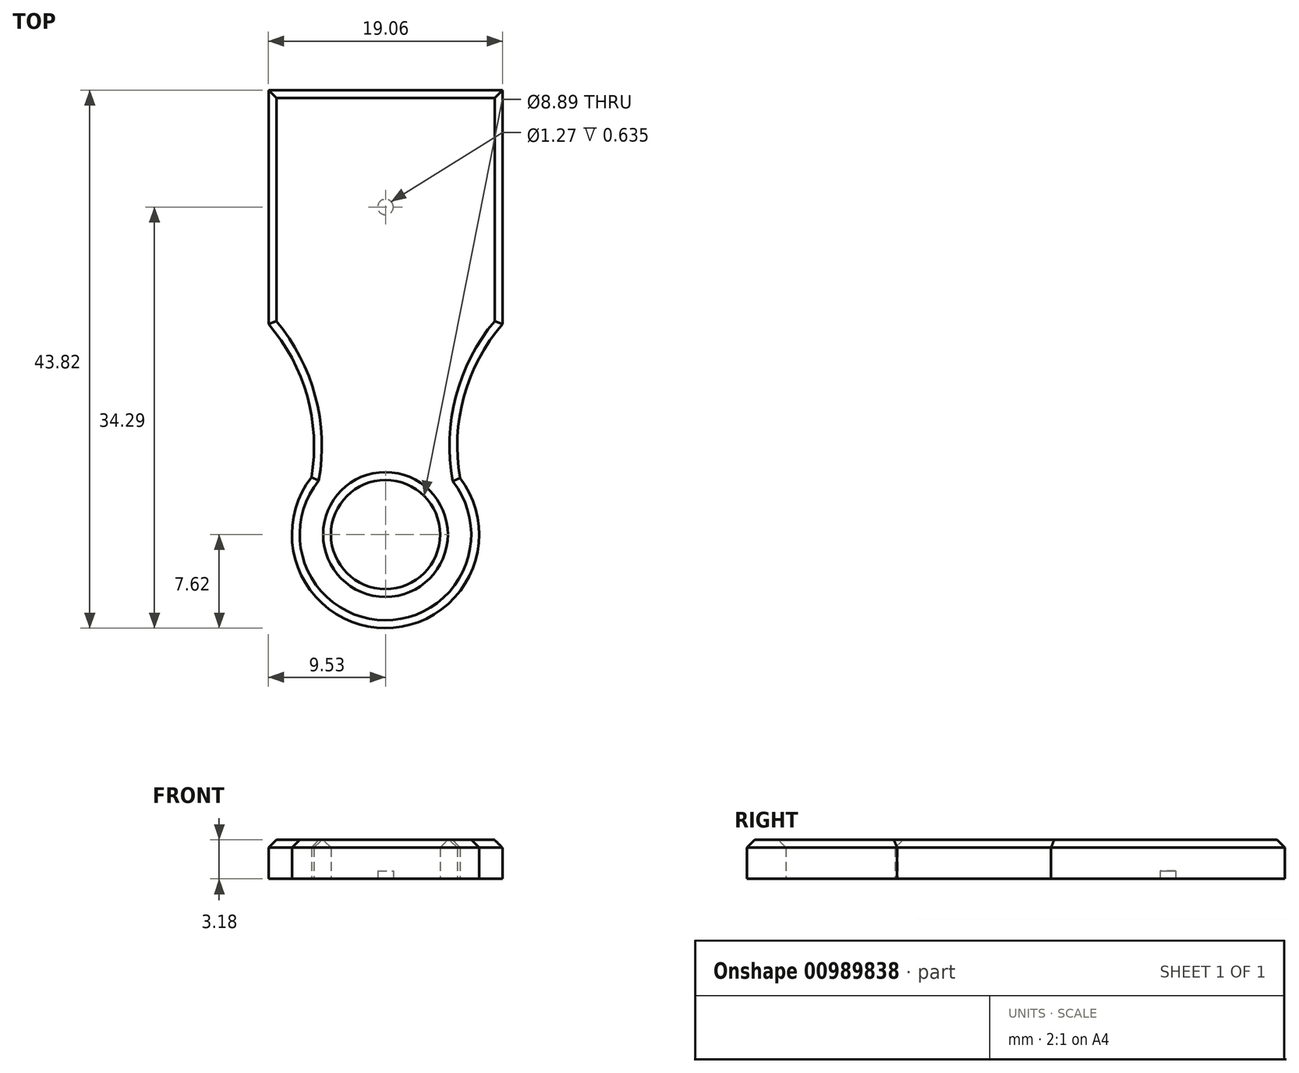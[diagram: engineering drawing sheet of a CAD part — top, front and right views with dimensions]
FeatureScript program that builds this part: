
annotation { "Feature Type Name" : "Feature", "Feature Type Description" : "" }
export const myFeature = defineFeature(function(context is Context, id is Id, definition is map)
    precondition{}
    {
        {
            var Q0;
            Q0=qCreatedBy(makeId("Top.planeOp"),FACE);
            var sketch = newSketch(context, id + "F0", { "sketchPlane" : qUnion([Q0])});
            skLineSegment(sketch, "E0.bottom", {"start": v(-9.52, 9.53) * mm, "end": v(9.53, 9.53) * mm});
            skLineSegment(sketch, "E0.top", {"start": v(-9.53, -9.53) * mm, "end": v(9.53, -9.53) * mm});
            skLineSegment(sketch, "E0.left", {"start": v(-9.52, 9.53) * mm, "end": v(-9.53, -9.53) * mm});
            skLineSegment(sketch, "E0.right", {"start": v(9.53, 9.53) * mm, "end": v(9.53, -9.53) * mm});
            skPoint(sketch, "E0.middle", {"position": v(0, 0) * mm});
            skCircle(sketch, "E1", {"center": v(0, -26.67) * mm, "radius": 7.62 * mm});
            skLineSegment(sketch, "E2", {"start": v(0, -26.67) * mm, "end": v(0, 0) * mm, "construction": true});
            skLineSegment(sketch, "E3", {"start": v(-7.62, -26.67) * mm, "end": v(-9.52, -9.52) * mm, "construction": true});
            skLineSegment(sketch, "E4", {"start": v(9.52, -9.53) * mm, "end": v(7.66, -26.67) * mm, "construction": true});
            skLineSegment(sketch, "E5", {"start": v(0, -9.53) * mm, "end": v(0, -19.05) * mm, "construction": true});
            skLineSegment(sketch, "E6", {"start": v(0, -19.05) * mm, "end": v(0, -13.97) * mm, "construction": true});
            skArc(sketch, "E7", {"start": v(-7.62, -26.67) * mm, "mid": v(-5.91, -17.8) * mm, "end": v(-9.52, -9.52) * mm});
            skArc(sketch, "E8", {"start": v(9.52, -9.53) * mm, "mid": v(5.94, -17.8) * mm, "end": v(7.66, -26.67) * mm});
            skCircle(sketch, "E9", {"center": v(0, -26.67) * mm, "radius": 4.45 * mm});
            skSolve(sketch);
        }
        {
            var Q0;
            Q0=makeQuery(id+"F0.imprint","IMPRINT",FACE,{"disambiguationData":[TD([[makeQuery(id+"F0.imprint","IMPRINT",EDGE,{"derivedFrom":sQuery(id+"F0.wireOp",EDGE,"E0.bottom")}),-1.0]])]});
            var Q1;
            {var subQ0=sQuery(id+"F0.wireOp",EDGE,"E0.top");Q1=makeQuery(id+"F0.imprint","IMPRINT",FACE,{"disambiguationData":[TD([[makeQuery(id+"F0.imprint","IMPRINT",EDGE,{"derivedFrom":subQ0}),-1.0]])]});}
            var Q2;
            {var subQ0=sQuery(id+"F0.wireOp",EDGE,"E8");var subQ1=sQuery(id+"F0.wireOp",EDGE,"E1");var subQ2=makeQuery(id+"F0.imprint","INTERSECT",VERTEX,{"disambiguationData":[OD(1.0)],"derivedFrom":[subQ1,subQ0]});Q2=makeQuery(id+"F0.imprint","IMPRINT",FACE,{"disambiguationData":[TD([[makeQuery(id+"F0.imprint","IMPRINT",EDGE,{"disambiguationData":[TD([[subQ2,-1.0]])],"derivedFrom":subQ1}),1.0]])]});}
            var Q3;
            {var subQ0=sQuery(id+"F0.wireOp",EDGE,"E7");var subQ1=sQuery(id+"F0.wireOp",EDGE,"E1");var subQ2=makeQuery(id+"F0.imprint","INTERSECT",VERTEX,{"disambiguationData":[OD(0.0)],"derivedFrom":[subQ1,subQ0]});Q3=makeQuery(id+"F0.imprint","IMPRINT",FACE,{"disambiguationData":[TD([[makeQuery(id+"F0.imprint","IMPRINT",EDGE,{"disambiguationData":[TD([[subQ2,1.0]])],"derivedFrom":subQ1}),1.0]])]});}
            var Q4;
            {var subQ0=sQuery(id+"F0.wireOp",EDGE,"E8");var subQ1=sQuery(id+"F0.wireOp",EDGE,"E1");var subQ2=makeQuery(id+"F0.imprint","INTERSECT",VERTEX,{"disambiguationData":[OD(0.0)],"derivedFrom":[subQ1,subQ0]});Q4=makeQuery(id+"F0.imprint","IMPRINT",FACE,{"disambiguationData":[TD([[makeQuery(id+"F0.imprint","IMPRINT",EDGE,{"disambiguationData":[TD([[subQ2,-1.0]])],"derivedFrom":subQ1}),1.0]])]});}
            extrude(context, id + "F1", {"entities" : qUnion([Q0, Q1, Q2, Q3, Q4]), "depth" : 3.17 * mm, "offsetDistance" : 25.4 * mm});
        }
        {
            var Q0;
            Q0=makeQuery(id+"F1.opExtrude","CAP_FACE",FACE,{"disambiguationData":[OSD([sQuery(id+"F0.wireOp",EDGE,"E0.bottom"),sQuery(id+"F0.wireOp",EDGE,"E0.left"),sQuery(id+"F0.wireOp",EDGE,"E0.right"),sQuery(id+"F0.wireOp",EDGE,"E1"),sQuery(id+"F0.wireOp",EDGE,"E7"),sQuery(id+"F0.wireOp",EDGE,"E8"),sQuery(id+"F0.wireOp",EDGE,"E9")])],"isStart":false});
            chamfer(context, id + "F2", {"entities" : qUnion([Q0]), "width" : 0.64 * mm, "tangentPropagation" : true});
        }
        {
            var Q0;
            Q0=makeQuery(id+"F1.opExtrude","CAP_FACE",FACE,{"disambiguationData":[OSD([sQuery(id+"F0.wireOp",EDGE,"E0.bottom"),sQuery(id+"F0.wireOp",EDGE,"E0.left"),sQuery(id+"F0.wireOp",EDGE,"E0.right"),sQuery(id+"F0.wireOp",EDGE,"E1"),sQuery(id+"F0.wireOp",EDGE,"E7"),sQuery(id+"F0.wireOp",EDGE,"E8"),sQuery(id+"F0.wireOp",EDGE,"E9")])],"isStart":true});
            var sketch = newSketch(context, id + "F3", { "sketchPlane" : qUnion([Q0])});
            skCircle(sketch, "E10", {"center": v(0, 0) * mm, "radius": 0.64 * mm});
            skSolve(sketch);
        }
        {
            var Q0;
            Q0=makeQuery(id+"F3.imprint","IMPRINT",FACE,{"disambiguationData":[TD([[makeQuery(id+"F3.imprint","IMPRINT",EDGE,{"derivedFrom":sQuery(id+"F3.wireOp",EDGE,"E10")}),1.0]])]});
            extrude(context, id + "F4", {"entities" : qUnion([Q0]), "operationType" : NewBodyOperationType.REMOVE, "oppositeDirection" : true, "depth" : 0.64 * mm, "offsetDistance" : 25.4 * mm});
        }
    });
